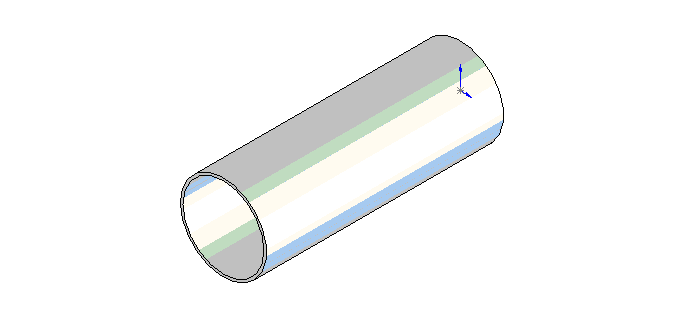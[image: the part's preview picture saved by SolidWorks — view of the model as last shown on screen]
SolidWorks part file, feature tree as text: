
SOLIDWORKS PART (.sldprt)
format: sldprt  version: not decoded by parser v0  size: 237,056 bytes
history: native  units: mm
features: plane x3, sketch x3, cut_extrude x2, extrude x1 + 1 further entry (+7 scaffold rows collapsed)
feature tree (17):
  scaffold x7  (default folders/planes/origin — collapsed)
  "Corps de surface"
  plane  "Face"
  plane  "Dessus"
  plane  "Droite"
  sketch  "Esquisse1"  dims[D1=80.0mm D2=75.2mm]
  extrude  "Extrusion1"  Depth=220mm
  sketch  "Esquisse2"  dims[c1.D1=125.0mm c1.D2=75.0mm c1.D3=20.0mm c2.D1=125.0mm c2.D2=75.0mm c2.D4=95.0mm c3.D1=50.0mm]
  cut_extrude  "Enlèv. mat.-Extru.2"  Depth=100mm
  sketch  "Esquisse3"  dims[c1.D1=90.0mm c1.D2=60.0mm c1.D3=22.5mm c2.D1=60.0mm c2.D2=90.0mm]
  cut_extrude  "Enlèv. mat.-Extru.3"  Depth=100mm
decode coverage: 6 of 6 modeling features carry decoded parameters; 1 rows unclassified (native names shown)
note: suppression state not decoded; provenance and decode notes live in map.json
